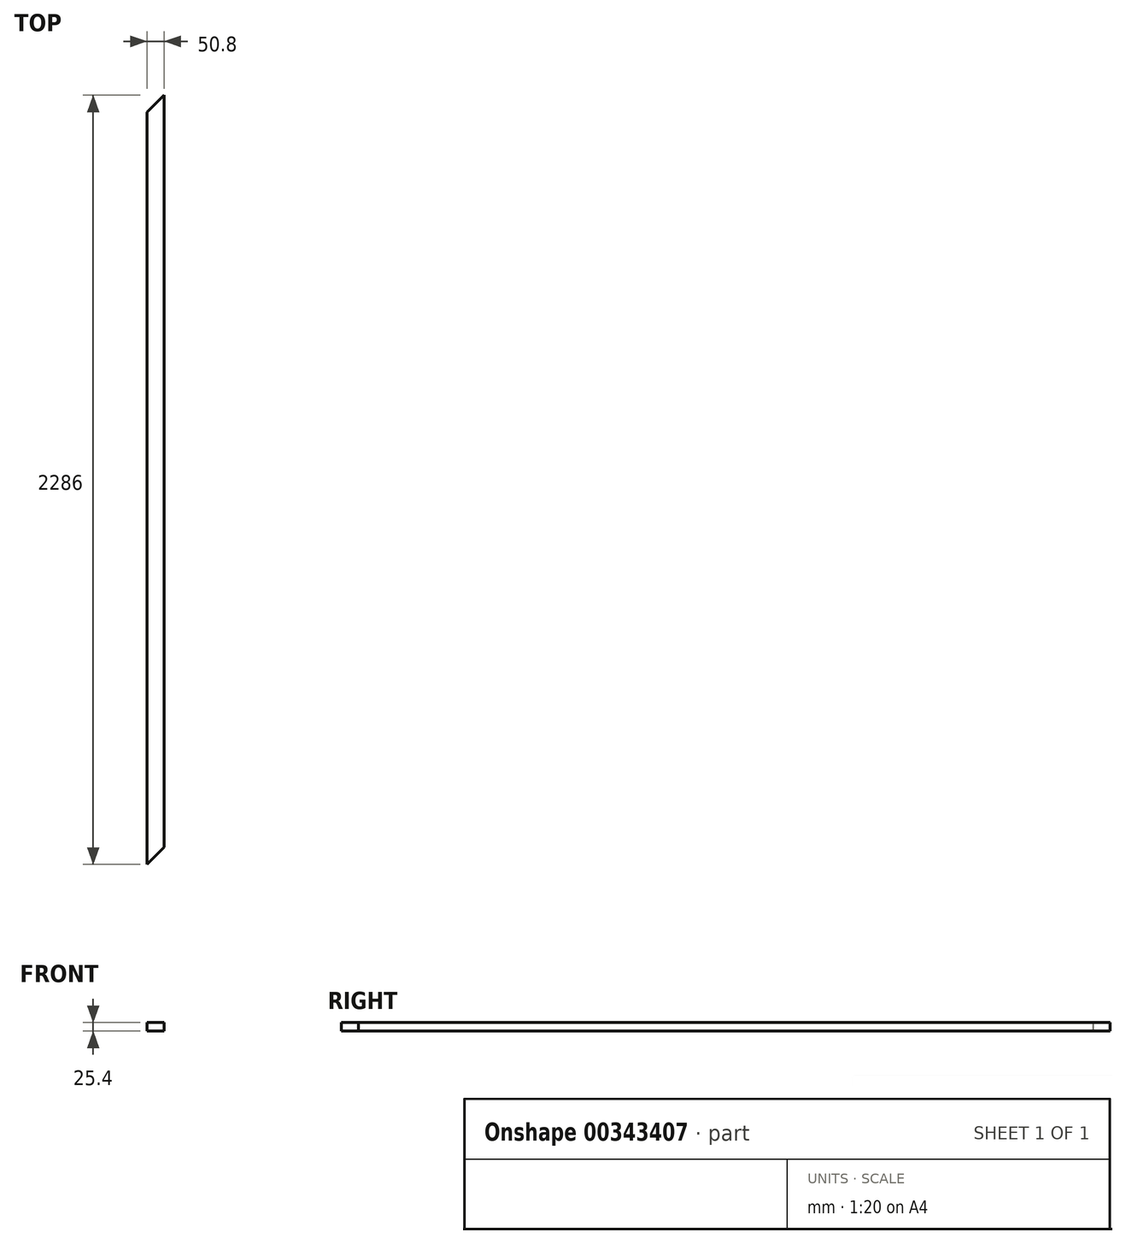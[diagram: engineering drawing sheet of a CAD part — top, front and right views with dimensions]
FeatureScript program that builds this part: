
annotation { "Feature Type Name" : "Feature", "Feature Type Description" : "" }
export const myFeature = defineFeature(function(context is Context, id is Id, definition is map)
    precondition{}
    {
        {
            var Q0;
            Q0=qCreatedBy(makeId("Front.planeOp"),FACE);
            var sketch = newSketch(context, id + "F0", { "sketchPlane" : qUnion([Q0])});
            skLineSegment(sketch, "E0.bottom", {"start": v(-23.05, 21.55) * mm, "end": v(-73.85, 21.55) * mm});
            skLineSegment(sketch, "E0.top", {"start": v(-23.05, 46.95) * mm, "end": v(-73.85, 46.95) * mm});
            skLineSegment(sketch, "E0.left", {"start": v(-23.05, 21.55) * mm, "end": v(-23.05, 46.95) * mm});
            skLineSegment(sketch, "E0.right", {"start": v(-73.85, 21.55) * mm, "end": v(-73.85, 46.95) * mm});
            skSolve(sketch);
        }
        {
            var Q0;
            Q0=makeQuery(id+"F0.imprint","IMPRINT",FACE,{"disambiguationData":[TD([[makeQuery(id+"F0.imprint","IMPRINT",EDGE,{"derivedFrom":sQuery(id+"F0.wireOp",EDGE,"E0.bottom")}),-1.0]])]});
            extrude(context, id + "F1", {"entities" : qUnion([Q0]), "depth" : 2286 * mm});
        }
        {
            var Q0;
            Q0=makeQuery(id+"F1.opExtrude","CAP_EDGE",EDGE,{"disambiguationData":[OSD([sQuery(id+"F0.wireOp",EDGE,"E0.left")])],"isStart":false});
            chamfer(context, id + "F2", {"entities" : qUnion([Q0]), "width" : 50.8 * mm, "tangentPropagation" : true});
        }
        {
            var Q0;
            Q0=makeQuery(id+"F1.opExtrude","CAP_EDGE",EDGE,{"disambiguationData":[OSD([sQuery(id+"F0.wireOp",EDGE,"E0.right")])],"isStart":true});
            chamfer(context, id + "F3", {"entities" : qUnion([Q0]), "width" : 50.8 * mm, "tangentPropagation" : true});
        }
    });
